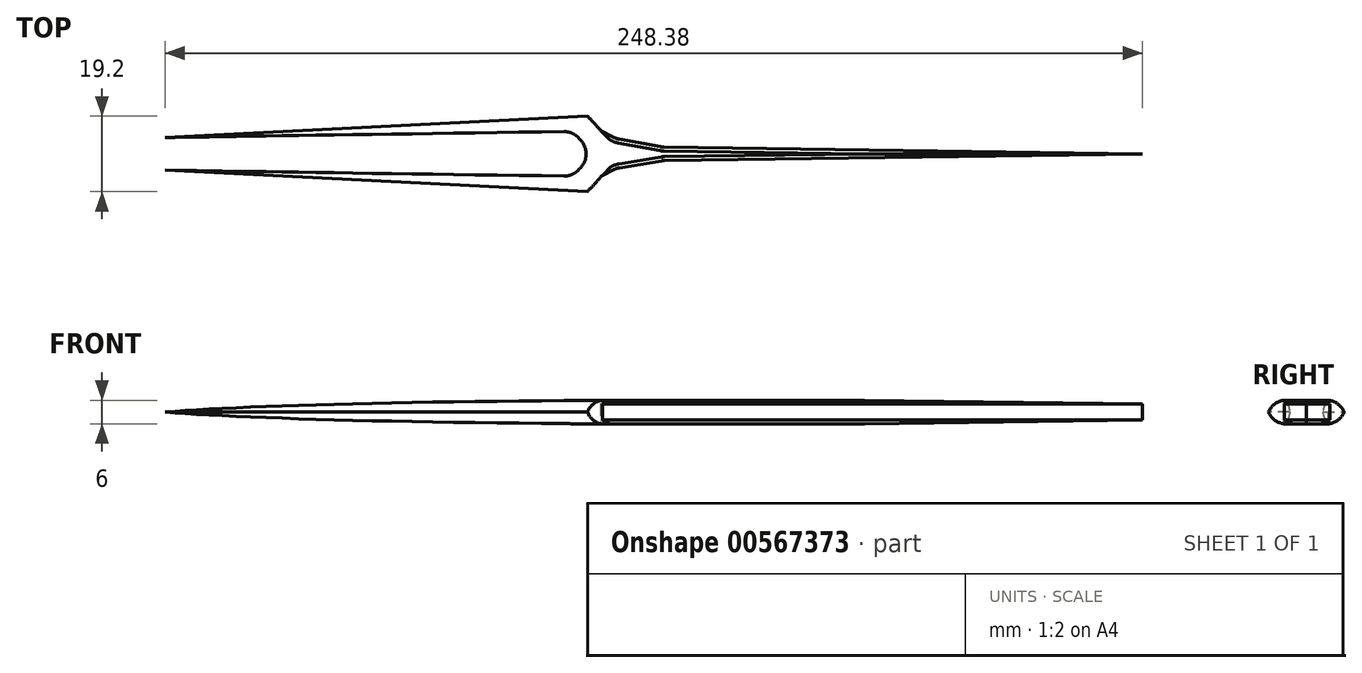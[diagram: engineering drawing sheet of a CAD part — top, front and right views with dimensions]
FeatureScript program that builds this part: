
annotation { "Feature Type Name" : "Feature", "Feature Type Description" : "" }
export const myFeature = defineFeature(function(context is Context, id is Id, definition is map)
    precondition{}
    {
        {
            var Q0;
            Q0=qCreatedBy(makeId("Top.planeOp"),FACE);
            var sketch = newSketch(context, id + "F0", { "sketchPlane" : qUnion([Q0])});
            skPoint(sketch, "E0.middle", {"position": v(0, 0) * mm});
            skLineSegment(sketch, "E1", {"start": v(-11.37, 2) * mm, "end": v(-11.37, -2) * mm});
            skPoint(sketch, "E2", {"position": v(-130, 4) * mm});
            skPoint(sketch, "E3", {"position": v(-130, -4) * mm});
            skLineSegment(sketch, "E4", {"start": v(-130, 4) * mm, "end": v(-11.37, 10) * mm});
            skLineSegment(sketch, "E5", {"start": v(-11.37, -10) * mm, "end": v(-130, -4) * mm});
            skLineSegment(sketch, "E6", {"start": v(-11.38, 10) * mm, "end": v(-7.66, 5.95) * mm});
            skLineSegment(sketch, "E7", {"start": v(-11.37, -10) * mm, "end": v(-7.26, -5.52) * mm});
            skLineSegment(sketch, "E8", {"start": v(-7.26, -5.52) * mm, "end": v(-3.63, -3.68) * mm});
            skLineSegment(sketch, "E9", {"start": v(-7.66, 5.95) * mm, "end": v(-3.83, 3.9) * mm});
            skLineSegment(sketch, "E10", {"start": v(-3.83, 3.9) * mm, "end": v(7.97, 1.73) * mm});
            skLineSegment(sketch, "E11", {"start": v(-3.63, -3.68) * mm, "end": v(8.2, -1.72) * mm});
            skLineSegment(sketch, "E12", {"start": v(-11.37, 2) * mm, "end": v(-14.76, 5.68) * mm});
            skLineSegment(sketch, "E13", {"start": v(-11.38, -2) * mm, "end": v(-14.76, -5.68) * mm});
            skLineSegment(sketch, "E14", {"start": v(-14.76, 5.68) * mm, "end": v(-130, 4) * mm});
            skLineSegment(sketch, "E15", {"start": v(-14.76, -5.68) * mm, "end": v(-130, -4) * mm});
            skPoint(sketch, "E16.orphan", {"position": v(-11.37, 0) * mm});
            skLineSegment(sketch, "E17.trimOffspring", {"start": v(8.2, -1.72) * mm, "end": v(130, 0) * mm});
            skLineSegment(sketch, "E18.trimOffspring", {"start": v(7.97, 1.73) * mm, "end": v(130, 0) * mm});
            skPoint(sketch, "E19.end.orphan", {"position": v(-3.94, 1.9) * mm});
            skPoint(sketch, "E20.orphan", {"position": v(0, 1.84) * mm});
            skPoint(sketch, "E21.orphan", {"position": v(0, -1.84) * mm});
            skPoint(sketch, "E22.orphan", {"position": v(-3.94, -1.9) * mm});
            skSolve(sketch);
        }
        {
            var Q0;
            Q0 = qSketchRegion(id + "F0", true);
            extrude(context, id + "F1", {"entities" : qUnion([Q0]), "depth" : 6 * mm, "offsetDistance" : 25 * mm});
        }
        {
            var Q0;
            Q0=makeQuery(id+"F1.opExtrude","CAP_EDGE",EDGE,{"disambiguationData":[OSD([sQuery(id+"F0.wireOp",EDGE,"E5")])],"isStart":false});
            var Q1;
            Q1=makeQuery(id+"F1.opExtrude","CAP_EDGE",EDGE,{"disambiguationData":[OSD([sQuery(id+"F0.wireOp",EDGE,"E5")])],"isStart":true});
            var Q2;
            Q2=makeQuery(id+"F1.opExtrude","CAP_EDGE",EDGE,{"disambiguationData":[OSD([sQuery(id+"F0.wireOp",EDGE,"E4")])],"isStart":true});
            var Q3;
            Q3=makeQuery(id+"F1.opExtrude","CAP_EDGE",EDGE,{"disambiguationData":[OSD([sQuery(id+"F0.wireOp",EDGE,"E4")])],"isStart":false});
            var Q4;
            Q4=makeQuery(id+"F1.opExtrude","SWEPT_EDGE",EDGE,{"disambiguationData":[OSD([sQuery(id+"F0.wireOp",EDGE,"E1"),sQuery(id+"F0.wireOp",EDGE,"E13")])]});
            var Q5;
            Q5=makeQuery(id+"F1.opExtrude","SWEPT_EDGE",EDGE,{"disambiguationData":[OSD([sQuery(id+"F0.wireOp",EDGE,"E1"),sQuery(id+"F0.wireOp",EDGE,"E12")])]});
            var Q6;
            Q6=makeQuery(id+"F1.opExtrude","SWEPT_EDGE",EDGE,{"disambiguationData":[OSD([sQuery(id+"F0.wireOp",EDGE,"E12"),sQuery(id+"F0.wireOp",EDGE,"E14")])]});
            var Q7;
            Q7=makeQuery(id+"F1.opExtrude","SWEPT_EDGE",EDGE,{"disambiguationData":[OSD([sQuery(id+"F0.wireOp",EDGE,"E13"),sQuery(id+"F0.wireOp",EDGE,"E15")])]});
            var Q8;
            Q8=makeQuery(id+"F1.opExtrude","SWEPT_EDGE",EDGE,{"disambiguationData":[OSD([sQuery(id+"F0.wireOp",EDGE,"E10"),sQuery(id+"F0.wireOp",EDGE,"E18.trimOffspring")])]});
            var Q9;
            Q9=makeQuery(id+"F1.opExtrude","SWEPT_EDGE",EDGE,{"disambiguationData":[OSD([sQuery(id+"F0.wireOp",EDGE,"E9"),sQuery(id+"F0.wireOp",EDGE,"E10")])]});
            var Q10;
            Q10=makeQuery(id+"F1.opExtrude","SWEPT_EDGE",EDGE,{"disambiguationData":[OSD([sQuery(id+"F0.wireOp",EDGE,"E8"),sQuery(id+"F0.wireOp",EDGE,"E11")])]});
            var Q11;
            Q11=makeQuery(id+"F1.opExtrude","SWEPT_EDGE",EDGE,{"disambiguationData":[OSD([sQuery(id+"F0.wireOp",EDGE,"E11"),sQuery(id+"F0.wireOp",EDGE,"E17.trimOffspring")])]});
            fillet(context, id + "F2", {"entities" : qUnion([Q0, Q1, Q2, Q3, Q4, Q5, Q6, Q7, Q8, Q9, Q10, Q11]), "radius" : 5 * mm, "tangentPropagation" : true, "allowEdgeOverflow" : false});
        }
        {
            var Q0;
            Q0=makeQuery(id+"F1.opExtrude","CAP_EDGE",EDGE,{"disambiguationData":[OSD([sQuery(id+"F0.wireOp",EDGE,"E17.trimOffspring")])],"isStart":false});
            var Q1;
            Q1=makeQuery(id+"F1.opExtrude","CAP_EDGE",EDGE,{"disambiguationData":[OSD([sQuery(id+"F0.wireOp",EDGE,"E18.trimOffspring")])],"isStart":false});
            var Q2;
            Q2=makeQuery(id+"F1.opExtrude","CAP_EDGE",EDGE,{"disambiguationData":[OSD([sQuery(id+"F0.wireOp",EDGE,"E17.trimOffspring")])],"isStart":true});
            var Q3;
            Q3=makeQuery(id+"F1.opExtrude","CAP_EDGE",EDGE,{"disambiguationData":[OSD([sQuery(id+"F0.wireOp",EDGE,"E18.trimOffspring")])],"isStart":true});
            chamfer(context, id + "F3", {"entities" : qUnion([Q0, Q1, Q2, Q3]), "width" : 1 * mm, "tangentPropagation" : true});
        }
    });
